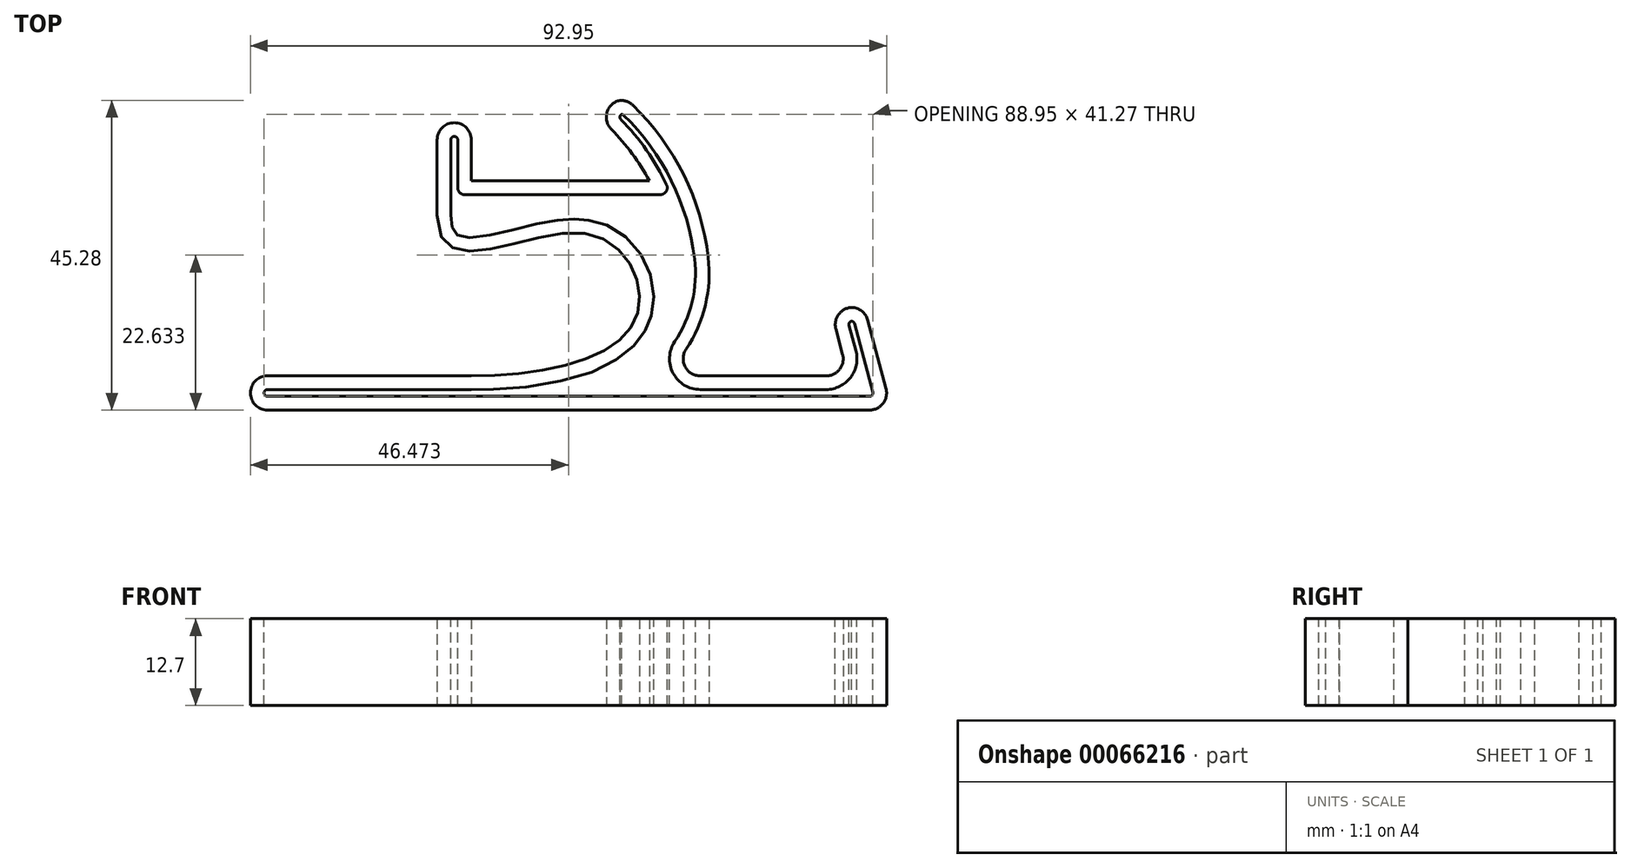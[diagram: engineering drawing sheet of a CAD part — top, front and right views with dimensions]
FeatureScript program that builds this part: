
annotation { "Feature Type Name" : "Feature", "Feature Type Description" : "" }
export const myFeature = defineFeature(function(context is Context, id is Id, definition is map)
    precondition{}
    {
        {
            var Q0;
            Q0=qCreatedBy(makeId("Top.planeOp"),FACE);
            var sketch = newSketch(context, id + "F0", { "sketchPlane" : qUnion([Q0])});
            skLineSegment(sketch, "E0", {"start": v(0, 0) * mm, "end": v(26, 0) * mm});
            skLineSegment(sketch, "E1", {"start": v(0, 0) * mm, "end": v(0, 8.87) * mm});
            skArc(sketch, "E2", {"start": v(26, 0) * mm, "mid": v(21.8, 6.1) * mm, "end": v(16.33, 11.06) * mm});
            skLineSegment(sketch, "E3.1", {"start": v(-5, -5) * mm, "end": v(-5, 8.2) * mm});
            skArc(sketch, "E3.2", {"start": v(30.18, -33.5) * mm, "mid": v(34.37, -9.49) * mm, "end": v(22.7, 11.91) * mm});
            skFitSpline(sketch, "E4", {"points": [v(-5, -5) * mm, v(16.13, -7.63) * mm, v(23.96, -20.25) * mm, v(0, -28.5) * mm], "startDerivative": vector(0, -92.19) * mm, "endDerivative": vector(-77.51, 0) * mm});
            skLineSegment(sketch, "E5", {"start": v(0, -28.5) * mm, "end": v(-32.28, -28.5) * mm});
            skLineSegment(sketch, "E6", {"start": v(30.18, -33.5) * mm, "end": v(-32.28, -33.5) * mm});
            skPoint(sketch, "E7.start.orphan", {"position": v(-45, -50.97) * mm});
            skPoint(sketch, "E8.orphan", {"position": v(0, -33.5) * mm});
            skLineSegment(sketch, "E9", {"start": v(-32.28, -28.5) * mm, "end": v(-32.28, -33.5) * mm});
            skLineSegment(sketch, "E10", {"start": v(22.7, 11.91) * mm, "end": v(16.33, 11.06) * mm});
            skPoint(sketch, "E11.orphan", {"position": v(0, 16.95) * mm});
            skLineSegment(sketch, "E12.trimOffspring", {"start": v(0, 8.87) * mm, "end": v(-5, 8.2) * mm});
            skPoint(sketch, "E13.orphan", {"position": v(-5, 21.39) * mm});
            skSolve(sketch);
        }
        {
            var Q0;
            Q0=makeQuery(id+"F0.imprint","IMPRINT",FACE,{"disambiguationData":[TD([[makeQuery(id+"F0.imprint","IMPRINT",EDGE,{"derivedFrom":sQuery(id+"F0.wireOp",EDGE,"E0")}),-1.0]])]});
            extrude(context, id + "F1", {"entities" : qUnion([Q0]), "depth" : 12.7 * mm});
        }
        {
            var Q0;
            Q0=makeQuery(id+"F1.opExtrude","SWEPT_EDGE",EDGE,{"disambiguationData":[OSD([sQuery(id+"F0.wireOp",EDGE,"E3.2"),sQuery(id+"F0.wireOp",EDGE,"E6")])]});
            fillet(context, id + "F2", {"entities" : qUnion([Q0]), "radius" : 20 * mm, "tangentPropagation" : true, "allowEdgeOverflow" : false});
        }
        {
            var Q0;
            Q0=makeQuery(id+"F1.opExtrude","SWEPT_EDGE",EDGE,{"disambiguationData":[OSD([sQuery(id+"F0.wireOp",EDGE,"E5"),sQuery(id+"F0.wireOp",EDGE,"E9")])]});
            var Q1;
            Q1=makeQuery(id+"F1.opExtrude","SWEPT_EDGE",EDGE,{"disambiguationData":[OSD([sQuery(id+"F0.wireOp",EDGE,"E6"),sQuery(id+"F0.wireOp",EDGE,"E9")])]});
            fillet(context, id + "F3", {"entities" : qUnion([Q0, Q1]), "radius" : 2.5 * mm, "tangentPropagation" : true, "allowEdgeOverflow" : false});
        }
        {
            var Q0;
            Q0=makeQuery(id+"F1.opExtrude","CAP_FACE",FACE,{"disambiguationData":[OSD([sQuery(id+"F0.wireOp",EDGE,"E0"),sQuery(id+"F0.wireOp",EDGE,"E1"),sQuery(id+"F0.wireOp",EDGE,"E2"),sQuery(id+"F0.wireOp",EDGE,"E3.1"),sQuery(id+"F0.wireOp",EDGE,"E3.2"),sQuery(id+"F0.wireOp",EDGE,"E4"),sQuery(id+"F0.wireOp",EDGE,"E5"),sQuery(id+"F0.wireOp",EDGE,"E6"),sQuery(id+"F0.wireOp",EDGE,"E9"),sQuery(id+"F0.wireOp",EDGE,"E10"),sQuery(id+"F0.wireOp",EDGE,"E12.trimOffspring")])],"isStart":false});
            var sketch = newSketch(context, id + "F4", { "sketchPlane" : qUnion([Q0])});
            skLineSegment(sketch, "E14", {"start": v(14.74, -33.5) * mm, "end": v(61.43, -33.5) * mm});
            skLineSegment(sketch, "E15", {"start": v(61.43, -33.5) * mm, "end": v(57.4, -18.5) * mm});
            skLineSegment(sketch, "E16", {"start": v(57.4, -18.5) * mm, "end": v(52.4, -18.5) * mm});
            skLineSegment(sketch, "E17", {"start": v(52.4, -18.5) * mm, "end": v(55.09, -28.5) * mm});
            skLineSegment(sketch, "E18", {"start": v(55.09, -28.5) * mm, "end": v(27.97, -28.5) * mm});
            skSolve(sketch);
        }
        {
            var Q0;
            {var subQ0=sQuery(id+"F4.wireOp",EDGE,"E14");Q0=makeQuery(id+"F4.imprint","IMPRINT",FACE,{"disambiguationData":[TD([[makeQuery(id+"F4.imprint","IMPRINT",EDGE,{"derivedFrom":subQ0}),1.0]])]});}
            var Q1;
            Q1=makeQuery(id+"F1.opExtrude","CAP_FACE",FACE,{"disambiguationData":[OSD([sQuery(id+"F0.wireOp",EDGE,"E0"),sQuery(id+"F0.wireOp",EDGE,"E1"),sQuery(id+"F0.wireOp",EDGE,"E2"),sQuery(id+"F0.wireOp",EDGE,"E3.1"),sQuery(id+"F0.wireOp",EDGE,"E3.2"),sQuery(id+"F0.wireOp",EDGE,"E4"),sQuery(id+"F0.wireOp",EDGE,"E5"),sQuery(id+"F0.wireOp",EDGE,"E6"),sQuery(id+"F0.wireOp",EDGE,"E9"),sQuery(id+"F0.wireOp",EDGE,"E10"),sQuery(id+"F0.wireOp",EDGE,"E12.trimOffspring")])],"isStart":true});
            extrude(context, id + "F5", {"entities" : qUnion([Q0]), "operationType" : NewBodyOperationType.ADD, "endBound" : BoundingType.UP_TO_SURFACE, "oppositeDirection" : true, "endBoundEntityFace" : qUnion([Q1]), "depth" : 25 * mm});
        }
        {
            var Q0;
            Q0=makeQuery(id+"F1.opExtrude","SWEPT_EDGE",EDGE,{"disambiguationData":[OSD([sQuery(id+"F0.wireOp",EDGE,"E2"),sQuery(id+"F0.wireOp",EDGE,"E10")])]});
            var Q1;
            Q1=makeQuery(id+"F1.opExtrude","SWEPT_EDGE",EDGE,{"disambiguationData":[OSD([sQuery(id+"F0.wireOp",EDGE,"E3.2"),sQuery(id+"F0.wireOp",EDGE,"E10")])]});
            var Q2;
            Q2=makeQuery(id+"F1.opExtrude","SWEPT_EDGE",EDGE,{"disambiguationData":[OSD([sQuery(id+"F0.wireOp",EDGE,"E1"),sQuery(id+"F0.wireOp",EDGE,"E12.trimOffspring")])]});
            var Q3;
            Q3=makeQuery(id+"F1.opExtrude","SWEPT_EDGE",EDGE,{"disambiguationData":[OSD([sQuery(id+"F0.wireOp",EDGE,"E3.1"),sQuery(id+"F0.wireOp",EDGE,"E12.trimOffspring")])]});
            var Q4;
            Q4=makeQuery(id+"F5.opExtrude","SWEPT_EDGE",EDGE,{"disambiguationData":[OSD([sQuery(id+"F4.wireOp",EDGE,"E16"),sQuery(id+"F4.wireOp",EDGE,"E17")])]});
            var Q5;
            Q5=makeQuery(id+"F5.opExtrude","SWEPT_EDGE",EDGE,{"disambiguationData":[OSD([sQuery(id+"F4.wireOp",EDGE,"E15"),sQuery(id+"F4.wireOp",EDGE,"E16")])]});
            var Q6;
            Q6=makeQuery(id+"F5.opExtrude","SWEPT_EDGE",EDGE,{"disambiguationData":[OSD([sQuery(id+"F4.wireOp",EDGE,"E17"),sQuery(id+"F4.wireOp",EDGE,"E18")])]});
            var Q7;
            Q7=makeQuery(id+"F5.opExtrude","SWEPT_EDGE",EDGE,{"disambiguationData":[OSD([sQuery(id+"F0.wireOp",EDGE,"E0"),sQuery(id+"F0.wireOp",EDGE,"E1"),sQuery(id+"F0.wireOp",EDGE,"E2"),sQuery(id+"F0.wireOp",EDGE,"E3.1"),sQuery(id+"F0.wireOp",EDGE,"E3.2"),sQuery(id+"F0.wireOp",EDGE,"E4"),sQuery(id+"F0.wireOp",EDGE,"E5"),sQuery(id+"F0.wireOp",EDGE,"E6"),sQuery(id+"F0.wireOp",EDGE,"E9"),sQuery(id+"F0.wireOp",EDGE,"E10"),sQuery(id+"F0.wireOp",EDGE,"E12.trimOffspring"),sQuery(id+"F4.wireOp",EDGE,"E18")])]});
            var Q8;
            Q8=makeQuery(id+"F5.opExtrude","SWEPT_EDGE",EDGE,{"disambiguationData":[OSD([sQuery(id+"F4.wireOp",EDGE,"E14"),sQuery(id+"F4.wireOp",EDGE,"E15")])]});
            fillet(context, id + "F6", {"entities" : qUnion([Q0, Q1, Q2, Q3, Q4, Q5, Q6, Q7, Q8]), "radius" : 2.5 * mm, "tangentPropagation" : true, "allowEdgeOverflow" : false});
        }
        {
            var Q0;
            {var subQ0=sQuery(id+"F0.wireOp",EDGE,"E12.trimOffspring");var subQ1=sQuery(id+"F0.wireOp",EDGE,"E10");var subQ2=sQuery(id+"F0.wireOp",EDGE,"E9");var subQ3=sQuery(id+"F0.wireOp",EDGE,"E6");var subQ4=sQuery(id+"F0.wireOp",EDGE,"E5");var subQ5=sQuery(id+"F0.wireOp",EDGE,"E4");var subQ6=sQuery(id+"F0.wireOp",EDGE,"E3.2");var subQ7=sQuery(id+"F0.wireOp",EDGE,"E3.1");var subQ8=sQuery(id+"F0.wireOp",EDGE,"E2");var subQ9=sQuery(id+"F0.wireOp",EDGE,"E1");var subQ10=sQuery(id+"F0.wireOp",EDGE,"E0");Q0=makeQuery(id+"F5.boolean.opBoolean","MERGE",FACE,{"derivedFrom":[makeQuery(id+"F1.opExtrude","CAP_FACE",FACE,{"disambiguationData":[OSD([subQ10,subQ9,subQ8,subQ7,subQ6,subQ5,subQ4,subQ3,subQ2,subQ1,subQ0])],"isStart":false}),makeQuery(id+"F5.opExtrude","CAP_FACE",FACE,{"disambiguationData":[OSD([subQ10,subQ9,subQ8,subQ7,subQ6,subQ5,subQ4,subQ3,subQ2,subQ1,subQ0,sQuery(id+"F4.wireOp",EDGE,"E14"),sQuery(id+"F4.wireOp",EDGE,"E15"),sQuery(id+"F4.wireOp",EDGE,"E16"),sQuery(id+"F4.wireOp",EDGE,"E17"),sQuery(id+"F4.wireOp",EDGE,"E18")])],"isStart":true})]});}
            var sketch = newSketch(context, id + "F7", { "sketchPlane" : qUnion([Q0])});
            skLineSegment(sketch, "E19.1", {"start": v(-37.28, -31) * mm, "end": v(-37.28, -31) * mm});
            skArc(sketch, "E20.0", {"start": v(32.61, -11.38) * mm, "mid": v(29.22, 0.03) * mm, "end": v(22.21, 9.64) * mm});
            skArc(sketch, "E20.1", {"start": v(29.7, -23.5) * mm, "mid": v(32.24, -17.7) * mm, "end": v(32.61, -11.38) * mm});
            skArc(sketch, "E20.2", {"start": v(33.45, -30.5) * mm, "mid": v(29.48, -28.12) * mm, "end": v(29.7, -23.5) * mm});
            skLineSegment(sketch, "E20.3", {"start": v(51.83, -30.5) * mm, "end": v(33.45, -30.5) * mm});
            skArc(sketch, "E20.4", {"start": v(56.18, -24.84) * mm, "mid": v(55.4, -28.74) * mm, "end": v(51.83, -30.5) * mm});
            skLineSegment(sketch, "E20.5", {"start": v(55.18, -21.13) * mm, "end": v(56.18, -24.84) * mm});
            skArc(sketch, "E20.6", {"start": v(58.17, -31.5) * mm, "mid": v(58.57, -31.3) * mm, "end": v(58.65, -30.87) * mm});
            skLineSegment(sketch, "E20.7", {"start": v(58.65, -30.87) * mm, "end": v(55.97, -20.87) * mm});
            skArc(sketch, "E20.8", {"start": v(55.97, -20.87) * mm, "mid": v(55.83, -20.63) * mm, "end": v(55.58, -20.5) * mm});
            skArc(sketch, "E20.9", {"start": v(55.58, -20.5) * mm, "mid": v(55.24, -20.73) * mm, "end": v(55.18, -21.13) * mm});
            skLineSegment(sketch, "E20.10", {"start": v(-29.78, -31.5) * mm, "end": v(58.17, -31.5) * mm});
            skArc(sketch, "E20.11", {"start": v(22.21, 9.64) * mm, "mid": v(22.1, 9.72) * mm, "end": v(21.98, 9.77) * mm});
            skArc(sketch, "E20.12", {"start": v(21.98, 9.77) * mm, "mid": v(21.72, 9.4) * mm, "end": v(21.86, 8.97) * mm});
            skArc(sketch, "E20.13", {"start": v(21.86, 8.97) * mm, "mid": v(26.04, 3.84) * mm, "end": v(29.15, -2) * mm});
            skLineSegment(sketch, "E20.14", {"start": v(29.15, -2) * mm, "end": v(-2, -2) * mm});
            skLineSegment(sketch, "E20.15", {"start": v(-2, -2) * mm, "end": v(-2, 6) * mm});
            skArc(sketch, "E20.16", {"start": v(-2, 6) * mm, "mid": v(-2.5, 6.5) * mm, "end": v(-3, 6) * mm});
            skLineSegment(sketch, "E20.17", {"start": v(-3, 6) * mm, "end": v(-3, -5) * mm});
            skFitSpline(sketch, "E20.18", {"points": [v(-3, -5) * mm, v(-3, -5.4) * mm, v(-2.95, -6.11) * mm, v(-2.78, -6.88) * mm, v(-2.56, -7.37) * mm, v(-2.34, -7.66) * mm, v(-2.1, -7.86) * mm, v(-1.75, -8.04) * mm, v(-1.25, -8.18) * mm, v(-0.34, -8.28) * mm, v(1.16, -8.2) * mm, v(3.36, -7.8) * mm, v(5.83, -7.2) * mm, v(8.44, -6.54) * mm, v(10.68, -6.04) * mm, v(12.48, -5.76) * mm, v(13.82, -5.61) * mm, v(14.94, -5.57) * mm, v(15.82, -5.6) * mm, v(16.71, -5.67) * mm, v(17.78, -5.85) * mm, v(19.4, -6.32) * mm, v(21.24, -7.22) * mm, v(23.08, -8.68) * mm, v(24.55, -10.44) * mm, v(25.64, -12.4) * mm, v(26.34, -14.5) * mm, v(26.64, -16.66) * mm, v(26.54, -18.47) * mm, v(26.23, -19.88) * mm, v(25.87, -20.92) * mm, v(25.4, -21.9) * mm, v(24.61, -23.12) * mm, v(23.4, -24.46) * mm, v(21.67, -25.8) * mm, v(19.05, -27.3) * mm, v(15.3, -28.7) * mm, v(10.31, -29.79) * mm, v(5.1, -30.38) * mm, v(1.66, -30.5) * mm, v(0, -30.5) * mm]});
            skLineSegment(sketch, "E20.19", {"start": v(0, -30.5) * mm, "end": v(-29.78, -30.5) * mm});
            skArc(sketch, "E20.20", {"start": v(-29.78, -30.5) * mm, "mid": v(-30.14, -30.65) * mm, "end": v(-30.28, -31) * mm});
            skLineSegment(sketch, "E20.21", {"start": v(-30.28, -31) * mm, "end": v(-30.28, -31) * mm});
            skArc(sketch, "E20.22", {"start": v(-30.28, -31) * mm, "mid": v(-30.14, -31.35) * mm, "end": v(-29.78, -31.5) * mm});
            skSolve(sketch);
        }
        {
            var Q0;
            Q0=makeQuery(id+"F7.imprint","IMPRINT",FACE,{"disambiguationData":[TD([[makeQuery(id+"F7.imprint","IMPRINT",EDGE,{"derivedFrom":sQuery(id+"F7.wireOp",EDGE,"83aad82b-2f1e-4f61-94e4-9ff0f7ecfbde.0")}),1.0]])]});
            var Q1;
            Q1=makeQuery(id+"F7.imprint","IMPRINT",FACE,{"disambiguationData":[TD([[makeQuery(id+"F7.imprint","IMPRINT",EDGE,{"derivedFrom":sQuery(id+"F7.wireOp",EDGE,"E20.0")}),1.0]])]});
            extrude(context, id + "F8", {"entities" : qUnion([Q0, Q1]), "operationType" : NewBodyOperationType.REMOVE, "endBound" : BoundingType.THROUGH_ALL, "oppositeDirection" : true, "depth" : 25 * mm});
        }
        {
            var Q0;
            Q0=makeQuery(id+"F8.boolean.opBoolean","COPY",EDGE,{"derivedFrom":makeQuery(id+"F8.opExtrude","SWEPT_EDGE",EDGE,{"disambiguationData":[OSD([sQuery(id+"F7.wireOp",EDGE,"E20.13"),sQuery(id+"F7.wireOp",EDGE,"E20.14")])]})});
            var Q1;
            Q1=makeQuery(id+"F8.boolean.opBoolean","COPY",EDGE,{"derivedFrom":makeQuery(id+"F8.opExtrude","SWEPT_EDGE",EDGE,{"disambiguationData":[OSD([sQuery(id+"F7.wireOp",EDGE,"E20.14"),sQuery(id+"F7.wireOp",EDGE,"E20.15")])]})});
            fillet(context, id + "F9", {"entities" : qUnion([Q0, Q1]), "radius" : 1 * mm, "tangentPropagation" : true, "allowEdgeOverflow" : false});
        }
    });
